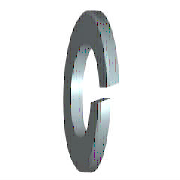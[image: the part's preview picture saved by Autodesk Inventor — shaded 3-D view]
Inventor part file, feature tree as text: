
AUTODESK INVENTOR PART (.ipt)
format: ipt  version: 2021 (Build 250183000, 183)  size: 123,904 bytes
history: native  units: mm (DEFAULTED — no unit token found)
features: sketch x2, extrude x1, other x1, plane x1
ambient origin geometry x6: Origin, YZ Plane, X Axis, Y Axis, Z Axis, Center Point
bodies: Solid1 (feature_tree), Body (feature_tree)
feature tree (5):
  extrude  "Cut"  Depth=47.0mm
  other  "Work Axis1"
  plane  "Work Plane1"
  sketch  "Sketch1"  dims[d0=27.0mm d1=47.0mm]
  sketch  "Sketch2"  dims[d2=10.0mm d3=0.0mm d4=2.0mm d5=2.0mm d6=90.0deg d7=10.0mm d8=0.0mm d9=0.0mm d10=0.0mm d11=0.0mm d12=0.0mm]
